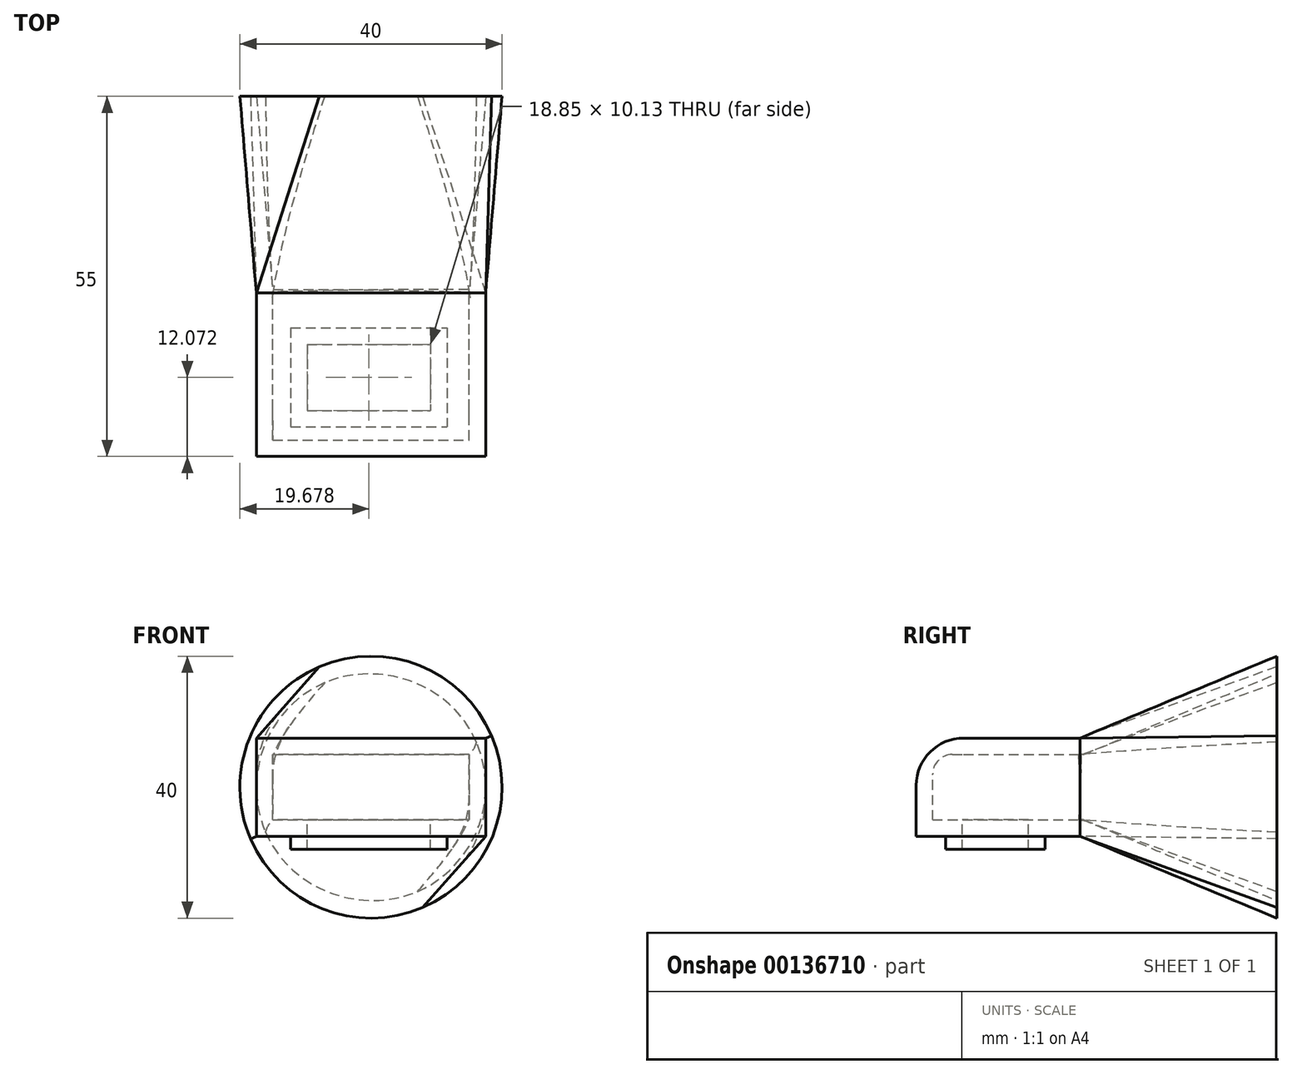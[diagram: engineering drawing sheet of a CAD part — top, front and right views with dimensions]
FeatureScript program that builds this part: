
annotation { "Feature Type Name" : "Feature", "Feature Type Description" : "" }
export const myFeature = defineFeature(function(context is Context, id is Id, definition is map)
    precondition{}
    {
        {
            var Q0;
            Q0=qCreatedBy(makeId("Front.planeOp"),FACE);
            var sketch = newSketch(context, id + "F0", { "sketchPlane" : qUnion([Q0])});
            skEllipse(sketch, "E0", {"center": v(0, 0) * mm, "majorRadius": 20 * mm, "minorRadius": 20 * mm, "majorAxis": v(1, -0.02)});
            skSolve(sketch);
        }
        {
            var Q0;
            Q0=qCreatedBy(makeId("Front.planeOp"),FACE);
            cPlane(context, id + "F1", {"entities" : qUnion([Q0]), "cplaneType" : CPlaneType.OFFSET, "offset" : 30 * mm, "width" : 150 * mm, "height" : 150 * mm});
        }
        {
            var Q0;
            Q0=qCreatedBy(id+"F1.planeOp",FACE);
            var sketch = newSketch(context, id + "F2", { "sketchPlane" : qUnion([Q0])});
            skLineSegment(sketch, "E1.bottom", {"start": v(17.5, 7.5) * mm, "end": v(-17.5, 7.5) * mm});
            skLineSegment(sketch, "E1.top", {"start": v(17.5, -7.5) * mm, "end": v(-17.5, -7.5) * mm});
            skLineSegment(sketch, "E1.left", {"start": v(17.5, 7.5) * mm, "end": v(17.5, -7.5) * mm});
            skLineSegment(sketch, "E1.right", {"start": v(-17.5, 7.5) * mm, "end": v(-17.5, -7.5) * mm});
            skPoint(sketch, "E1.middle", {"position": v(0, 0) * mm});
            skSolve(sketch);
        }
        {
            var Q0;
            Q0 = qSketchRegion(id + "F0", true);
            var Q1;
            Q1 = qSketchRegion(id + "F2", true);
            loft(context, id + "F3", {"sheetProfilesArray" : [{ "sheetProfileEntities" : qUnion([Q0]) }, { "sheetProfileEntities" : qUnion([Q1]) }]});
        }
        {
            var Q0;
            Q0=makeQuery(id+"F3.opLoft","CAP_FACE",FACE,{"disambiguationData":[OSD([makeQuery(id+"F2.imprint","IMPRINT",FACE,{"disambiguationData":[TD([[makeQuery(id+"F2.imprint","IMPRINT",EDGE,{"derivedFrom":sQuery(id+"F2.wireOp",EDGE,"E1.bottom")}),1.0]])]})])],"isStart":true});
            extrude(context, id + "F4", {"entities" : qUnion([Q0]), "operationType" : NewBodyOperationType.ADD, "depth" : 25 * mm});
        }
        {
            var Q0;
            Q0=makeQuery(id+"F4.opExtrude","SWEPT_FACE",FACE,{"disambiguationData":[OSD([sQuery(id+"F2.wireOp",EDGE,"E1.top"),sQuery(id+"F2.wireOp",EDGE,"E1.left"),sQuery(id+"F2.wireOp",EDGE,"E1.right")])]});
            var sketch = newSketch(context, id + "F5", { "sketchPlane" : qUnion([Q0])});
            skLineSegment(sketch, "E2.bottom", {"start": v(-12.25, 35.36) * mm, "end": v(11.6, 35.36) * mm});
            skLineSegment(sketch, "E2.top", {"start": v(-12.25, 50.5) * mm, "end": v(11.6, 50.5) * mm});
            skLineSegment(sketch, "E2.left", {"start": v(-12.25, 35.36) * mm, "end": v(-12.25, 50.5) * mm});
            skLineSegment(sketch, "E2.right", {"start": v(11.6, 35.36) * mm, "end": v(11.6, 50.5) * mm});
            skSolve(sketch);
        }
        {
            var Q0;
            Q0 = qSketchRegion(id + "F5", true);
            extrude(context, id + "F6", {"entities" : qUnion([Q0]), "operationType" : NewBodyOperationType.ADD, "depth" : 2 * mm});
        }
        {
            var Q0;
            Q0=makeQuery(id+"F6.opExtrude","CAP_FACE",FACE,{"disambiguationData":[OSD([sQuery(id+"F5.wireOp",EDGE,"E2.bottom"),sQuery(id+"F5.wireOp",EDGE,"E2.top"),sQuery(id+"F5.wireOp",EDGE,"E2.left"),sQuery(id+"F5.wireOp",EDGE,"E2.right")])],"isStart":false});
            var Q1;
            Q1=makeQuery(id+"F3.opLoft","CAP_FACE",FACE,{"disambiguationData":[OSD([makeQuery(id+"F0.imprint","IMPRINT",FACE,{"disambiguationData":[TD([[makeQuery(id+"F0.imprint","IMPRINT",EDGE,{"derivedFrom":sQuery(id+"F0.wireOp",EDGE,"E0")}),1.0]])]})])],"isStart":true});
            var Q2;
            Q2=makeQuery(id+"F3.opLoft","SWEPT_BODY",BODY,{"disambiguationData":[OSD([makeQuery(id+"F0.imprint","IMPRINT",FACE,{"disambiguationData":[TD([[makeQuery(id+"F0.imprint","IMPRINT",EDGE,{"derivedFrom":sQuery(id+"F0.wireOp",EDGE,"E0")}),1.0]])]}),makeQuery(id+"F2.imprint","IMPRINT",FACE,{"disambiguationData":[TD([[makeQuery(id+"F2.imprint","IMPRINT",EDGE,{"derivedFrom":sQuery(id+"F2.wireOp",EDGE,"E1.bottom")}),1.0]])]})])]});
            shell(context, id + "F7", {"entities" : qUnion([Q0, Q1]), "parts" : qUnion([Q2]), "thickness" : 2.5 * mm});
        }
        {
            var Q0;
            Q0=makeQuery(id+"F4.opExtrude","CAP_EDGE",EDGE,{"disambiguationData":[OSD([sQuery(id+"F2.wireOp",EDGE,"E1.bottom"),sQuery(id+"F2.wireOp",EDGE,"E1.left"),sQuery(id+"F2.wireOp",EDGE,"E1.right")])],"isStart":false});
            fillet(context, id + "F8", {"entities" : qUnion([Q0]), "radius" : 7.23 * mm, "tangentPropagation" : true, "allowEdgeOverflow" : false});
        }
        {
            var Q0;
            {var subQ0=sQuery(id+"F2.wireOp",EDGE,"E1.right");var subQ1=sQuery(id+"F2.wireOp",EDGE,"E1.left");var subQ2=sQuery(id+"F2.wireOp",EDGE,"E1.bottom");Q0=makeQuery(id+"F7.opShell","OFFSET_EDGE",EDGE,{"disambiguationData":[OSD([subQ2,subQ1,subQ0]),TDD([makeQuery(id+"F4.opExtrude","CAP_EDGE",EDGE,{"disambiguationData":[OSD([subQ2,subQ1,subQ0])],"isStart":false})])]});}
            fillet(context, id + "F9", {"entities" : qUnion([Q0]), "radius" : 3 * mm, "tangentPropagation" : true, "allowEdgeOverflow" : false});
        }
    });
